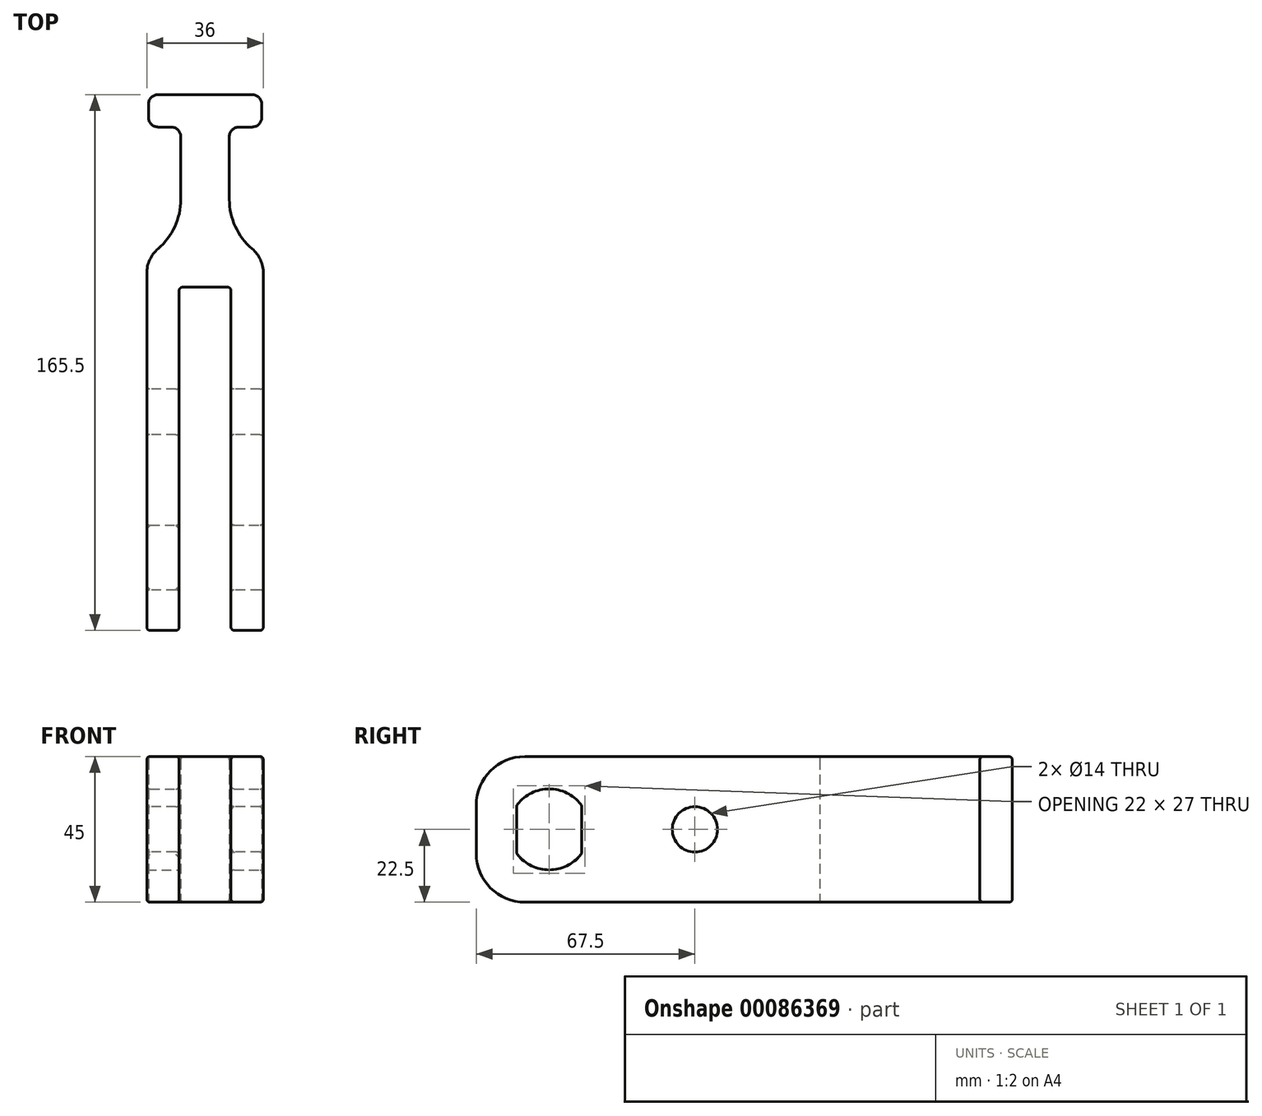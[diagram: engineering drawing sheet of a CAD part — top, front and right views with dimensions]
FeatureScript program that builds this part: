
annotation { "Feature Type Name" : "Feature", "Feature Type Description" : "" }
export const myFeature = defineFeature(function(context is Context, id is Id, definition is map)
    precondition{}
    {
        {
            var Q0;
            Q0=qCreatedBy(makeId("Top.planeOp"),FACE);
            var sketch = newSketch(context, id + "F0", { "sketchPlane" : qUnion([Q0])});
            skLineSegment(sketch, "E0.bottom", {"start": v(7.5, 82.5) * mm, "end": v(-7.5, 82.5) * mm});
            skLineSegment(sketch, "E0.top", {"start": v(7.5, -82.5) * mm, "end": v(-7.5, -82.5) * mm});
            skLineSegment(sketch, "E0.left", {"start": v(7.5, 82.5) * mm, "end": v(7.5, -82.5) * mm});
            skLineSegment(sketch, "E0.right", {"start": v(-7.5, 82.5) * mm, "end": v(-7.5, -82.5) * mm});
            skPoint(sketch, "E0.middle", {"position": v(0, 0) * mm});
            skLineSegment(sketch, "E1.bottom", {"start": v(7.5, 12.5) * mm, "end": v(52.5, 12.5) * mm});
            skLineSegment(sketch, "E1.top", {"start": v(7.5, -12.5) * mm, "end": v(52.5, -12.5) * mm});
            skLineSegment(sketch, "E1.left", {"start": v(7.5, 12.5) * mm, "end": v(7.5, -12.5) * mm});
            skLineSegment(sketch, "E1.right", {"start": v(52.5, 12.5) * mm, "end": v(52.5, -12.5) * mm});
            skPoint(sketch, "E1.middle", {"position": v(30, 0) * mm});
            skLineSegment(sketch, "E2.bottom", {"start": v(-7.5, 12.5) * mm, "end": v(-52.5, 12.5) * mm});
            skLineSegment(sketch, "E2.top", {"start": v(-7.5, -12.5) * mm, "end": v(-52.5, -12.5) * mm});
            skLineSegment(sketch, "E2.left", {"start": v(-7.5, 12.5) * mm, "end": v(-7.5, -12.5) * mm});
            skLineSegment(sketch, "E2.right", {"start": v(-52.5, 12.5) * mm, "end": v(-52.5, -12.5) * mm});
            skPoint(sketch, "E2.middle", {"position": v(-30, 0) * mm});
            skLineSegment(sketch, "E3.0", {"start": v(-8, 83) * mm, "end": v(-8, -82.5) * mm});
            skLineSegment(sketch, "E3.1", {"start": v(8, 83) * mm, "end": v(-8, 83) * mm});
            skLineSegment(sketch, "E3.2", {"start": v(8, 83) * mm, "end": v(8, -82.5) * mm});
            skLineSegment(sketch, "E4", {"start": v(-8, -22.5) * mm, "end": v(-18, -22.5) * mm});
            skLineSegment(sketch, "E5", {"start": v(-18, -22.5) * mm, "end": v(-18, 93) * mm});
            skLineSegment(sketch, "E6", {"start": v(-18, 93) * mm, "end": v(18, 93) * mm});
            skLineSegment(sketch, "E7", {"start": v(18, 93) * mm, "end": v(18, -22.5) * mm});
            skLineSegment(sketch, "E8", {"start": v(18, -22.5) * mm, "end": v(8, -22.5) * mm});
            skLineSegment(sketch, "E9", {"start": v(-7.5, 82.5) * mm, "end": v(-7.5, 138) * mm});
            skLineSegment(sketch, "E10", {"start": v(-7.5, 138) * mm, "end": v(7.5, 138) * mm});
            skLineSegment(sketch, "E11", {"start": v(7.5, 138) * mm, "end": v(7.5, 82.5) * mm});
            skLineSegment(sketch, "E12.bottom", {"start": v(17.5, 143) * mm, "end": v(-17.5, 143) * mm});
            skLineSegment(sketch, "E12.top", {"start": v(17.5, 133) * mm, "end": v(-17.5, 133) * mm});
            skLineSegment(sketch, "E12.left", {"start": v(17.5, 143) * mm, "end": v(17.5, 133) * mm});
            skLineSegment(sketch, "E12.right", {"start": v(-17.5, 143) * mm, "end": v(-17.5, 133) * mm});
            skPoint(sketch, "E12.middle", {"position": v(0, 138) * mm});
            skLineSegment(sketch, "E13", {"start": v(-8, 83) * mm, "end": v(-8, 83.5) * mm});
            skLineSegment(sketch, "E14", {"start": v(-8, 83.5) * mm, "end": v(8, 83.5) * mm});
            skLineSegment(sketch, "E15", {"start": v(8, 83.5) * mm, "end": v(8, 83) * mm});
            skSolve(sketch);
        }
        {
            var Q0;
            {var subQ5=sQuery(id+"F0.wireOp",EDGE,"E4");Q0=makeQuery(id+"F0.imprint","IMPRINT",FACE,{"disambiguationData":[TD([[makeQuery(id+"F0.imprint","IMPRINT",EDGE,{"derivedFrom":subQ5}),-1.0]])]});}
            var Q1;
            {var subQ0=sQuery(id+"F0.wireOp",EDGE,"E5");var subQ1=sQuery(id+"F0.wireOp",EDGE,"E2.bottom");var subQ2=makeQuery(id+"F0.imprint","INTERSECT",VERTEX,{"derivedFrom":[subQ1,subQ0]});Q1=makeQuery(id+"F0.imprint","IMPRINT",FACE,{"disambiguationData":[TD([[makeQuery(id+"F0.imprint","IMPRINT",EDGE,{"disambiguationData":[TD([[subQ2,1.0]])],"derivedFrom":subQ1}),1.0]])]});}
            var Q2;
            {var subQ5=sQuery(id+"F0.wireOp",EDGE,"E13");Q2=makeQuery(id+"F0.imprint","IMPRINT",FACE,{"disambiguationData":[TD([[makeQuery(id+"F0.imprint","IMPRINT",EDGE,{"derivedFrom":subQ5}),1.0]])]});}
            var Q3;
            {var subQ0=sQuery(id+"F0.wireOp",EDGE,"E9");var subQ1=sQuery(id+"F0.wireOp",EDGE,"E6");var subQ2=makeQuery(id+"F0.imprint","INTERSECT",VERTEX,{"derivedFrom":[subQ1,subQ0]});Q3=makeQuery(id+"F0.imprint","IMPRINT",FACE,{"disambiguationData":[TD([[makeQuery(id+"F0.imprint","IMPRINT",EDGE,{"disambiguationData":[TD([[subQ2,-1.0]])],"derivedFrom":subQ1}),-1.0]])]});}
            var Q4;
            {var subQ0=sQuery(id+"F0.wireOp",EDGE,"E9");var subQ1=sQuery(id+"F0.wireOp",EDGE,"E6");var subQ2=makeQuery(id+"F0.imprint","INTERSECT",VERTEX,{"derivedFrom":[subQ1,subQ0]});Q4=makeQuery(id+"F0.imprint","IMPRINT",FACE,{"disambiguationData":[TD([[makeQuery(id+"F0.imprint","IMPRINT",EDGE,{"disambiguationData":[TD([[subQ2,-1.0]])],"derivedFrom":subQ1}),1.0]])]});}
            var Q5;
            {var subQ5=sQuery(id+"F0.wireOp",EDGE,"E15");Q5=makeQuery(id+"F0.imprint","IMPRINT",FACE,{"disambiguationData":[TD([[makeQuery(id+"F0.imprint","IMPRINT",EDGE,{"derivedFrom":subQ5}),1.0]])]});}
            var Q6;
            {var subQ0=sQuery(id+"F0.wireOp",EDGE,"E7");var subQ1=sQuery(id+"F0.wireOp",EDGE,"E1.bottom");var subQ2=makeQuery(id+"F0.imprint","INTERSECT",VERTEX,{"derivedFrom":[subQ1,subQ0]});Q6=makeQuery(id+"F0.imprint","IMPRINT",FACE,{"disambiguationData":[TD([[makeQuery(id+"F0.imprint","IMPRINT",EDGE,{"disambiguationData":[TD([[subQ2,1.0]])],"derivedFrom":subQ1}),-1.0]])]});}
            var Q7;
            {var subQ5=sQuery(id+"F0.wireOp",EDGE,"E8");Q7=makeQuery(id+"F0.imprint","IMPRINT",FACE,{"disambiguationData":[TD([[makeQuery(id+"F0.imprint","IMPRINT",EDGE,{"derivedFrom":subQ5}),-1.0]])]});}
            var Q8;
            {var subQ0=sQuery(id+"F0.wireOp",EDGE,"E10");Q8=makeQuery(id+"F0.imprint","IMPRINT",FACE,{"disambiguationData":[TD([[makeQuery(id+"F0.imprint","IMPRINT",EDGE,{"derivedFrom":subQ0}),-1.0]])]});}
            var Q9;
            {var subQ1=sQuery(id+"F0.wireOp",EDGE,"E10");Q9=makeQuery(id+"F0.imprint","IMPRINT",FACE,{"disambiguationData":[TD([[makeQuery(id+"F0.imprint","IMPRINT",EDGE,{"derivedFrom":subQ1}),1.0]])]});}
            extrude(context, id + "F1", {"entities" : qUnion([Q0, Q1, Q2, Q3, Q4, Q5, Q6, Q7, Q8, Q9]), "depth" : 45 * mm, "offsetDistance" : 25 * mm});
        }
        {
            var Q0;
            Q0=makeQuery(id+"F1.opExtrude","CAP_EDGE",EDGE,{"disambiguationData":[OSD([sQuery(id+"F0.wireOp",EDGE,"E4")])],"isStart":false});
            var Q1;
            Q1=makeQuery(id+"F1.opExtrude","CAP_EDGE",EDGE,{"disambiguationData":[OSD([sQuery(id+"F0.wireOp",EDGE,"E4")])],"isStart":true});
            var Q2;
            Q2=makeQuery(id+"F1.opExtrude","CAP_EDGE",EDGE,{"disambiguationData":[OSD([sQuery(id+"F0.wireOp",EDGE,"E8")])],"isStart":false});
            var Q3;
            Q3=makeQuery(id+"F1.opExtrude","CAP_EDGE",EDGE,{"disambiguationData":[OSD([sQuery(id+"F0.wireOp",EDGE,"E8")])],"isStart":true});
            fillet(context, id + "F2", {"entities" : qUnion([Q0, Q1, Q2, Q3]), "radius" : 15 * mm, "tangentPropagation" : true, "allowEdgeOverflow" : false});
        }
        {
            var Q0;
            Q0=makeQuery(id+"F1.opExtrude","SWEPT_FACE",FACE,{"disambiguationData":[OSD([sQuery(id+"F0.wireOp",EDGE,"E7")])]});
            var sketch = newSketch(context, id + "F3", { "sketchPlane" : qUnion([Q0])});
            skCircle(sketch, "E16", {"center": v(0, 22.5) * mm, "radius": 22.5 * mm});
            skCircle(sketch, "E17", {"center": v(0, 22.5) * mm, "radius": 12.5 * mm});
            skLineSegment(sketch, "E18.bottom", {"start": v(10, 37.5) * mm, "end": v(-10, 37.5) * mm});
            skLineSegment(sketch, "E18.top", {"start": v(10, 7.5) * mm, "end": v(-10, 7.5) * mm});
            skLineSegment(sketch, "E18.left", {"start": v(10, 37.5) * mm, "end": v(10, 7.5) * mm});
            skLineSegment(sketch, "E18.right", {"start": v(-10, 37.5) * mm, "end": v(-10, 7.5) * mm});
            skSolve(sketch);
        }
        {
            var Q0;
            {var subQ0=sQuery(id+"F3.wireOp",EDGE,"E18.right");var subQ1=sQuery(id+"F3.wireOp",EDGE,"E17");var subQ2=makeQuery(id+"F3.imprint","INTERSECT",VERTEX,{"disambiguationData":[OD(0.0)],"derivedFrom":[subQ1,subQ0]});Q0=makeQuery(id+"F3.imprint","IMPRINT",FACE,{"disambiguationData":[TD([[makeQuery(id+"F3.imprint","IMPRINT",EDGE,{"disambiguationData":[TD([[subQ2,1.0]])],"derivedFrom":subQ1}),1.0]])]});}
            extrude(context, id + "F4", {"entities" : qUnion([Q0]), "operationType" : NewBodyOperationType.REMOVE, "endBound" : BoundingType.THROUGH_ALL, "oppositeDirection" : true, "depth" : 25 * mm, "offsetDistance" : 25 * mm});
        }
        {
            var Q0;
            Q0=makeQuery(id+"F1.opExtrude","SWEPT_EDGE",EDGE,{"disambiguationData":[OSD([sQuery(id+"F0.wireOp",EDGE,"E6"),sQuery(id+"F0.wireOp",EDGE,"E9")])]});
            var Q1;
            Q1=makeQuery(id+"F1.opExtrude","SWEPT_EDGE",EDGE,{"disambiguationData":[OSD([sQuery(id+"F0.wireOp",EDGE,"E6"),sQuery(id+"F0.wireOp",EDGE,"E11")])]});
            fillet(context, id + "F5", {"entities" : qUnion([Q0, Q1]), "radius" : 20 * mm, "tangentPropagation" : true, "allowEdgeOverflow" : false});
        }
        {
            var Q0;
            Q0=makeQuery(id+"F5.opFillet","BLEND_EDGE",EDGE,{"blendedFrom":[makeQuery(id+"F1.opExtrude","SWEPT_EDGE",EDGE,{"disambiguationData":[OSD([sQuery(id+"F0.wireOp",EDGE,"E6"),sQuery(id+"F0.wireOp",EDGE,"E11")])]}),makeQuery(id+"F1.opExtrude","SWEPT_FACE",FACE,{"disambiguationData":[OSD([sQuery(id+"F0.wireOp",EDGE,"E7")])]})],"blendedInto":[makeQuery(id+"F1.opExtrude","SWEPT_FACE",FACE,{"disambiguationData":[OSD([sQuery(id+"F0.wireOp",EDGE,"E7")])]})]});
            var Q1;
            Q1=makeQuery(id+"F5.opFillet","BLEND_EDGE",EDGE,{"blendedFrom":[makeQuery(id+"F1.opExtrude","SWEPT_EDGE",EDGE,{"disambiguationData":[OSD([sQuery(id+"F0.wireOp",EDGE,"E6"),sQuery(id+"F0.wireOp",EDGE,"E9")])]}),makeQuery(id+"F1.opExtrude","SWEPT_FACE",FACE,{"disambiguationData":[OSD([sQuery(id+"F0.wireOp",EDGE,"E5")])]})],"blendedInto":[makeQuery(id+"F1.opExtrude","SWEPT_FACE",FACE,{"disambiguationData":[OSD([sQuery(id+"F0.wireOp",EDGE,"E5")])]})]});
            fillet(context, id + "F6", {"entities" : qUnion([Q0, Q1]), "radius" : 10 * mm, "tangentPropagation" : true, "allowEdgeOverflow" : false});
        }
        {
            var Q0;
            Q0=makeQuery(id+"F1.opExtrude","SWEPT_EDGE",EDGE,{"disambiguationData":[OSD([sQuery(id+"F0.wireOp",EDGE,"E9"),sQuery(id+"F0.wireOp",EDGE,"E12.top")])]});
            var Q1;
            Q1=makeQuery(id+"F1.opExtrude","SWEPT_EDGE",EDGE,{"disambiguationData":[OSD([sQuery(id+"F0.wireOp",EDGE,"E12.top"),sQuery(id+"F0.wireOp",EDGE,"E12.right")])]});
            var Q2;
            Q2=makeQuery(id+"F1.opExtrude","SWEPT_EDGE",EDGE,{"disambiguationData":[OSD([sQuery(id+"F0.wireOp",EDGE,"E12.bottom"),sQuery(id+"F0.wireOp",EDGE,"E12.right")])]});
            var Q3;
            Q3=makeQuery(id+"F1.opExtrude","SWEPT_EDGE",EDGE,{"disambiguationData":[OSD([sQuery(id+"F0.wireOp",EDGE,"E11"),sQuery(id+"F0.wireOp",EDGE,"E12.top")])]});
            var Q4;
            Q4=makeQuery(id+"F1.opExtrude","SWEPT_EDGE",EDGE,{"disambiguationData":[OSD([sQuery(id+"F0.wireOp",EDGE,"E12.top"),sQuery(id+"F0.wireOp",EDGE,"E12.left")])]});
            var Q5;
            Q5=makeQuery(id+"F1.opExtrude","SWEPT_EDGE",EDGE,{"disambiguationData":[OSD([sQuery(id+"F0.wireOp",EDGE,"E12.bottom"),sQuery(id+"F0.wireOp",EDGE,"E12.left")])]});
            fillet(context, id + "F7", {"entities" : qUnion([Q0, Q1, Q2, Q3, Q4, Q5]), "radius" : 3 * mm, "tangentPropagation" : true, "allowEdgeOverflow" : false});
        }
        {
            var Q0;
            Q0=makeQuery(id+"F1.opExtrude","SWEPT_FACE",FACE,{"disambiguationData":[OSD([sQuery(id+"F0.wireOp",EDGE,"E4")])]});
            var Q1;
            Q1=makeQuery(id+"F1.opExtrude","SWEPT_FACE",FACE,{"disambiguationData":[OSD([sQuery(id+"F0.wireOp",EDGE,"E8")])]});
            var Q2;
            {var subQ1=sQuery(id+"F3.wireOp",EDGE,"E18.right");var subQ2=sQuery(id+"F3.wireOp",EDGE,"E17");Q2=makeQuery(id+"F4.boolean.opBoolean","COPY",FACE,{"disambiguationData":[TD([makeQuery(id+"F1.opExtrude","SWEPT_FACE",FACE,{"disambiguationData":[OSD([sQuery(id+"F0.wireOp",EDGE,"E3.2")])]})])],"derivedFrom":makeQuery(id+"F4.opExtrude","SWEPT_FACE",FACE,{"disambiguationData":[OSD([subQ2]),TDD([makeQuery(id+"F3.imprint","IMPRINT",EDGE,{"disambiguationData":[TD([[makeQuery(id+"F3.imprint","INTERSECT",VERTEX,{"disambiguationData":[OD(1.0)],"derivedFrom":[subQ2,subQ1]}),-1.0]])],"derivedFrom":subQ2})])]})});}
            var Q3;
            {var subQ0=sQuery(id+"F3.wireOp",EDGE,"E18.right");Q3=makeQuery(id+"F4.boolean.opBoolean","COPY",FACE,{"disambiguationData":[TD([makeQuery(id+"F1.opExtrude","SWEPT_FACE",FACE,{"disambiguationData":[OSD([sQuery(id+"F0.wireOp",EDGE,"E3.2")])]})])],"derivedFrom":makeQuery(id+"F4.opExtrude","SWEPT_FACE",FACE,{"disambiguationData":[OSD([subQ0])]})});}
            var Q4;
            {var subQ1=sQuery(id+"F3.wireOp",EDGE,"E18.right");var subQ2=sQuery(id+"F3.wireOp",EDGE,"E17");Q4=makeQuery(id+"F4.boolean.opBoolean","COPY",FACE,{"disambiguationData":[TD([makeQuery(id+"F1.opExtrude","SWEPT_FACE",FACE,{"disambiguationData":[OSD([sQuery(id+"F0.wireOp",EDGE,"E3.2")])]})])],"derivedFrom":makeQuery(id+"F4.opExtrude","SWEPT_FACE",FACE,{"disambiguationData":[OSD([subQ2]),TDD([makeQuery(id+"F3.imprint","IMPRINT",EDGE,{"disambiguationData":[TD([[makeQuery(id+"F3.imprint","INTERSECT",VERTEX,{"disambiguationData":[OD(0.0)],"derivedFrom":[subQ2,subQ1]}),1.0]])],"derivedFrom":subQ2})])]})});}
            var Q5;
            {var subQ0=sQuery(id+"F3.wireOp",EDGE,"E18.right");Q5=makeQuery(id+"F4.boolean.opBoolean","COPY",FACE,{"disambiguationData":[TD([makeQuery(id+"F1.opExtrude","SWEPT_FACE",FACE,{"disambiguationData":[OSD([sQuery(id+"F0.wireOp",EDGE,"E3.0")])]})])],"derivedFrom":makeQuery(id+"F4.opExtrude","SWEPT_FACE",FACE,{"disambiguationData":[OSD([subQ0])]})});}
            var Q6;
            {var subQ0=sQuery(id+"F3.wireOp",EDGE,"E18.right");var subQ2=sQuery(id+"F3.wireOp",EDGE,"E17");Q6=makeQuery(id+"F4.boolean.opBoolean","COPY",FACE,{"disambiguationData":[TD([makeQuery(id+"F1.opExtrude","SWEPT_FACE",FACE,{"disambiguationData":[OSD([sQuery(id+"F0.wireOp",EDGE,"E3.0")])]})])],"derivedFrom":makeQuery(id+"F4.opExtrude","SWEPT_FACE",FACE,{"disambiguationData":[OSD([subQ2]),TDD([makeQuery(id+"F3.imprint","IMPRINT",EDGE,{"disambiguationData":[TD([[makeQuery(id+"F3.imprint","INTERSECT",VERTEX,{"disambiguationData":[OD(0.0)],"derivedFrom":[subQ2,subQ0]}),1.0]])],"derivedFrom":subQ2})])]})});}
            var Q7;
            {var subQ2=sQuery(id+"F3.wireOp",EDGE,"E18.left");Q7=makeQuery(id+"F4.boolean.opBoolean","COPY",FACE,{"disambiguationData":[TD([makeQuery(id+"F1.opExtrude","SWEPT_FACE",FACE,{"disambiguationData":[OSD([sQuery(id+"F0.wireOp",EDGE,"E3.0")])]})])],"derivedFrom":makeQuery(id+"F4.opExtrude","SWEPT_FACE",FACE,{"disambiguationData":[OSD([subQ2])]})});}
            var Q8;
            Q8=makeQuery(id+"F1.opExtrude","SWEPT_FACE",FACE,{"disambiguationData":[OSD([sQuery(id+"F0.wireOp",EDGE,"E3.1")])]});
            var Q9;
            Q9=makeQuery(id+"F1.opExtrude","SWEPT_FACE",FACE,{"disambiguationData":[OSD([sQuery(id+"F0.wireOp",EDGE,"E14")])]});
            fillet(context, id + "F8", {"entities" : qUnion([Q0, Q1, Q2, Q3, Q4, Q5, Q6, Q7, Q8, Q9]), "radius" : 1 * mm, "tangentPropagation" : true, "allowEdgeOverflow" : false});
        }
        {
            var Q0;
            Q0=makeQuery(id+"F1.opExtrude","SWEPT_FACE",FACE,{"disambiguationData":[OSD([sQuery(id+"F0.wireOp",EDGE,"E5")])]});
            var sketch = newSketch(context, id + "F9", { "sketchPlane" : qUnion([Q0])});
            skLineSegment(sketch, "E19", {"start": v(0, 22.5) * mm, "end": v(-45, 22.5) * mm, "construction": true});
            skCircle(sketch, "E20", {"center": v(-45, 22.5) * mm, "radius": 7 * mm});
            skSolve(sketch);
        }
        {
            var Q0;
            Q0 = qSketchRegion(id + "F9", true);
            extrude(context, id + "F10", {"entities" : qUnion([Q0]), "operationType" : NewBodyOperationType.REMOVE, "endBound" : BoundingType.THROUGH_ALL, "oppositeDirection" : true, "depth" : 25 * mm, "offsetDistance" : 25 * mm});
        }
        {
            var Q0;
            Q0=makeQuery(id+"F10.boolean.opBoolean","COPY",FACE,{"disambiguationData":[TD([makeQuery(id+"F1.opExtrude","SWEPT_FACE",FACE,{"disambiguationData":[OSD([sQuery(id+"F0.wireOp",EDGE,"E3.2")])]})])],"derivedFrom":makeQuery(id+"F10.opExtrude","SWEPT_FACE",FACE,{"disambiguationData":[OSD([sQuery(id+"F9.wireOp",EDGE,"E20")])]})});
            var Q1;
            Q1=makeQuery(id+"F10.boolean.opBoolean","COPY",FACE,{"disambiguationData":[TD([makeQuery(id+"F1.opExtrude","SWEPT_FACE",FACE,{"disambiguationData":[OSD([sQuery(id+"F0.wireOp",EDGE,"E3.0")])]})])],"derivedFrom":makeQuery(id+"F10.opExtrude","SWEPT_FACE",FACE,{"disambiguationData":[OSD([sQuery(id+"F9.wireOp",EDGE,"E20")])]})});
            fillet(context, id + "F11", {"entities" : qUnion([Q0, Q1]), "radius" : 1 * mm, "tangentPropagation" : true, "allowEdgeOverflow" : false});
        }
    });
